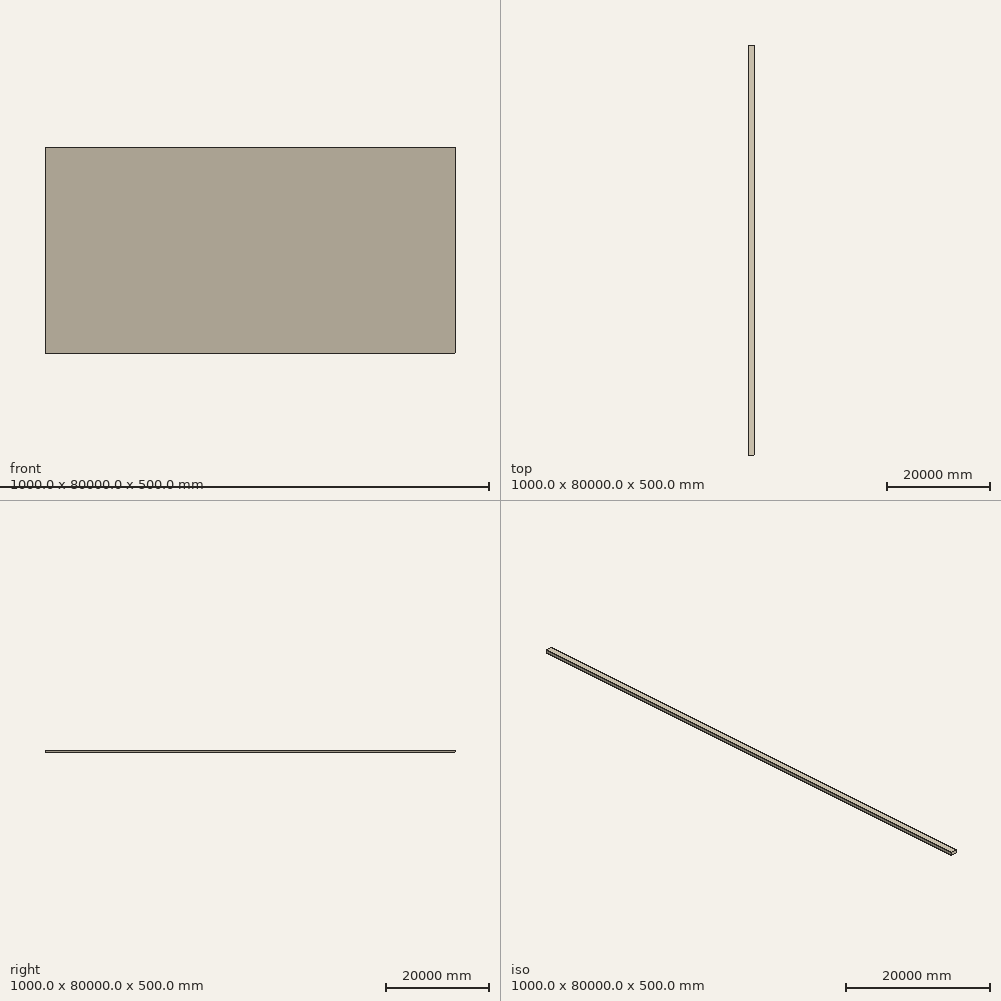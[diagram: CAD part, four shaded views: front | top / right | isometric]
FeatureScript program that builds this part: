
annotation { "Feature Type Name" : "Feature", "Feature Type Description" : "" }
export const myFeature = defineFeature(function(context is Context, id is Id, definition is map)
    precondition{}
    {
        {
            var Q0;
            Q0=qCreatedBy(makeId("Front.planeOp"),FACE);
            var sketch = newSketch(context, id + "F0", { "sketchPlane" : qUnion([Q0])});
            skLineSegment(sketch, "E0.bottom", {"start": v(-501.76, 50.47) * mm, "end": v(498.24, 50.47) * mm});
            skLineSegment(sketch, "E0.top", {"start": v(-501.76, -449.53) * mm, "end": v(498.24, -449.53) * mm});
            skLineSegment(sketch, "E0.left", {"start": v(-501.76, 50.47) * mm, "end": v(-501.76, -449.53) * mm});
            skLineSegment(sketch, "E0.right", {"start": v(498.24, 50.47) * mm, "end": v(498.24, -449.53) * mm});
            skSolve(sketch);
        }
        {
            var Q0;
            Q0 = qSketchRegion(id + "F0", true);
            extrude(context, id + "F1", {"entities" : qUnion([Q0]), "depth" : 80000 * mm, "offsetDistance" : 25 * mm});
        }
    });
